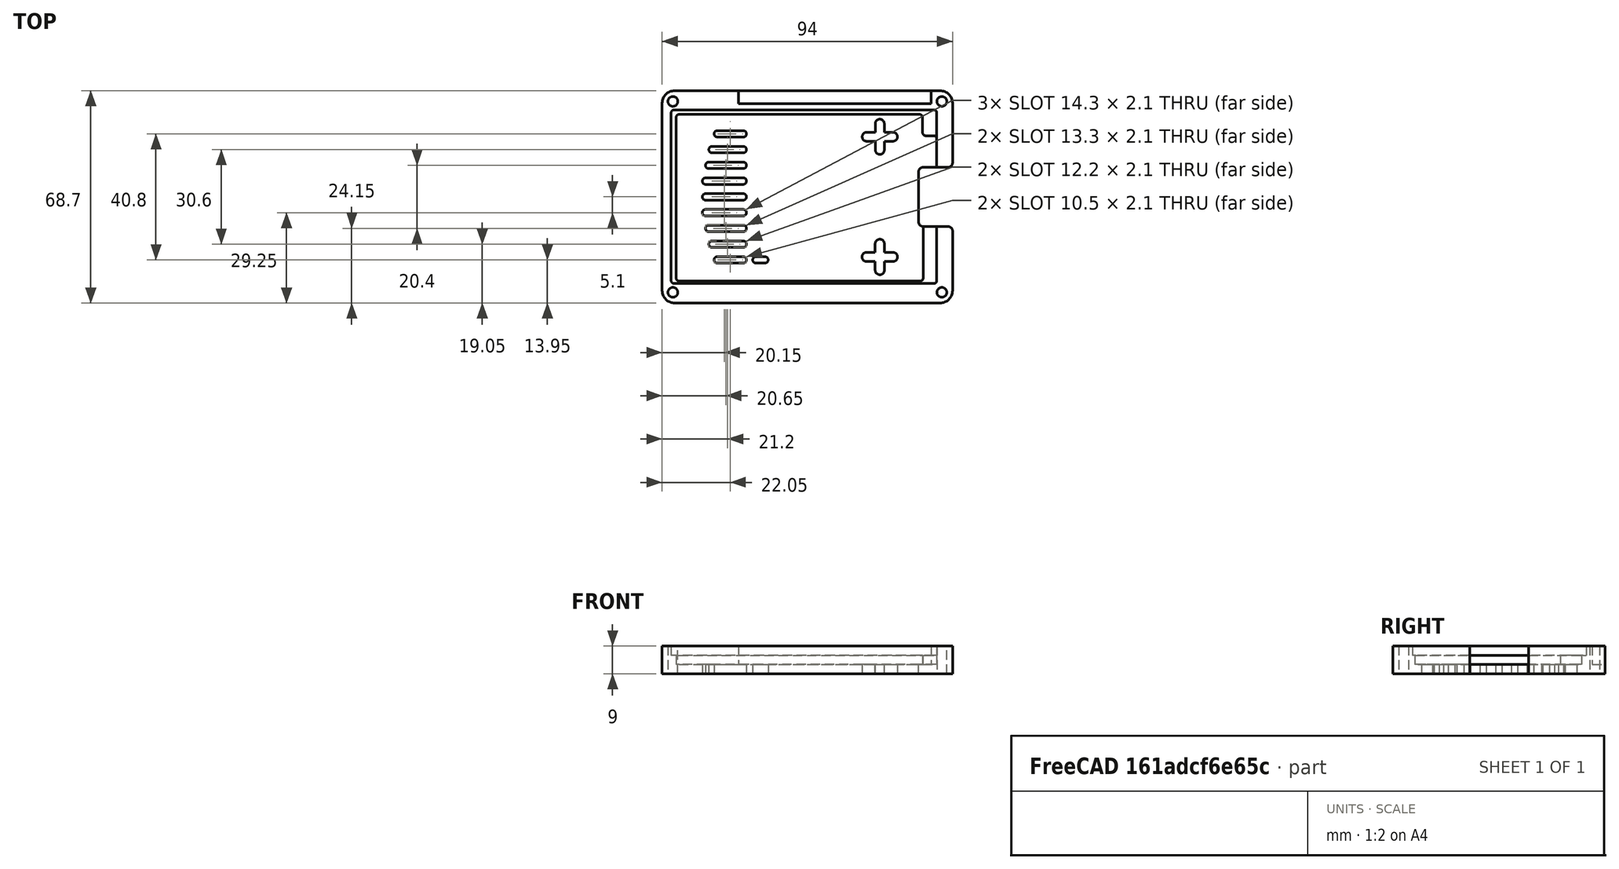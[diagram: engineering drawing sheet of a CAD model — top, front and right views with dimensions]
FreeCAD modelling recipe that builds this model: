
FCSTD DOCUMENT  (FreeCAD 0.19R24267 +148 (Git))
Label: 3. Lage
License: All rights reserved
LicenseURL: http://en.wikipedia.org/wiki/All_rights_reserved
objects: TechDraw::DrawViewDimension×23, Sketcher::SketchObject×3, TechDraw::DrawProjGroupItem×3, PartDesign::Pocket×2, PartDesign::Pad×1, PartDesign::Fillet×1, PartDesign::Body×1, TechDraw::DrawSVGTemplate×1, TechDraw::DrawProjGroup×1, TechDraw::DrawPage×1
note: 12 computed .brp shape members not serialized (recipe doc carries the construction recipe); baked Part::Feature solids carry a one-line shape summary decoded from their .brp

FEATURE [Sketcher::SketchObject] Sketch
  FullyConstrained = true
  MapMode = 5
  Support = -> [XY_Plane]
  sketch-geometry (97):
    g0: LineSegment StartX=0 StartY=0 StartZ=0 EndX=94 EndY=0 EndZ=0
    g1: LineSegment StartX=94 StartY=68.7 StartZ=0 EndX=0 EndY=68.7 EndZ=0
    g2: LineSegment StartX=0 StartY=68.7 StartZ=0 EndX=0 EndY=0 EndZ=0
    g3: GeomPoint X=47 Y=34.35 Z=0
    g4: Circle CenterX=3.45 CenterY=65.25 CenterZ=0 NormalX=0 NormalY=0 NormalZ=1 AngleXU=0 Radius=1.6
    g5: Circle CenterX=90.55 CenterY=65.25 CenterZ=0 NormalX=0 NormalY=0 NormalZ=1 AngleXU=0 Radius=1.6
    g6: Circle CenterX=90.55 CenterY=3.45 CenterZ=0 NormalX=0 NormalY=0 NormalZ=1 AngleXU=0 Radius=1.6
    g7: Circle CenterX=3.45 CenterY=3.45 CenterZ=0 NormalX=0 NormalY=0 NormalZ=1 AngleXU=0 Radius=1.6
    g8: LineSegment StartX=0 StartY=34.35 StartZ=0 EndX=94 EndY=34.35 EndZ=0
    g9: ArcOfCircle CenterX=70.45 CenterY=10.65 CenterZ=0 NormalX=0 NormalY=0 NormalZ=1 AngleXU=0 Radius=1.5 StartAngle=3.14159 EndAngle=6.28319
    g10: ArcOfCircle CenterX=74.7 CenterY=14.9 CenterZ=0 NormalX=0 NormalY=0 NormalZ=1 AngleXU=0 Radius=1.5 StartAngle=4.71239 EndAngle=7.85398
    g11: ArcOfCircle CenterX=70.45 CenterY=19.15 CenterZ=0 NormalX=0 NormalY=0 NormalZ=1 AngleXU=0 Radius=1.5 StartAngle=0 EndAngle=3.14159
    g12: ArcOfCircle CenterX=66.2 CenterY=14.9 CenterZ=0 NormalX=0 NormalY=0 NormalZ=1 AngleXU=0 Radius=1.5 StartAngle=1.5708 EndAngle=4.71239
    g13: LineSegment StartX=66.2 StartY=16.4 StartZ=0 EndX=68.95 EndY=16.4 EndZ=0
    g14: LineSegment StartX=68.95 StartY=16.4 StartZ=0 EndX=68.95 EndY=19.15 EndZ=0
    g15: LineSegment StartX=71.95 StartY=19.15 StartZ=0 EndX=71.95 EndY=16.4 EndZ=0
    g16: LineSegment StartX=71.95 StartY=16.4 StartZ=0 EndX=74.7 EndY=16.4 EndZ=0
    g17: LineSegment StartX=74.7 StartY=13.4 StartZ=0 EndX=71.95 EndY=13.4 EndZ=0
    g18: LineSegment StartX=71.95 StartY=13.4 StartZ=0 EndX=71.95 EndY=10.65 EndZ=0
    g19: LineSegment StartX=68.95 StartY=10.65 StartZ=0 EndX=68.95 EndY=13.4 EndZ=0
    g20: LineSegment StartX=68.95 StartY=13.4 StartZ=0 EndX=66.2 EndY=13.4 EndZ=0
    g21: ArcOfCircle CenterX=70.45 CenterY=49.55 CenterZ=0 NormalX=0 NormalY=0 NormalZ=1 AngleXU=0 Radius=1.45 StartAngle=3.14159 EndAngle=6.28319
    g22: ArcOfCircle CenterX=74.7 CenterY=53.8 CenterZ=0 NormalX=0 NormalY=0 NormalZ=1 AngleXU=0 Radius=1.45 StartAngle=4.71239 EndAngle=7.85398
    g23: ArcOfCircle CenterX=70.45 CenterY=58.05 CenterZ=0 NormalX=0 NormalY=0 NormalZ=1 AngleXU=0 Radius=1.45 StartAngle=7e-16 EndAngle=3.14159
    g24: ArcOfCircle CenterX=66.2 CenterY=53.8 CenterZ=0 NormalX=0 NormalY=0 NormalZ=1 AngleXU=0 Radius=1.45 StartAngle=1.5708 EndAngle=4.71239
    g25: LineSegment StartX=66.2 StartY=55.25 StartZ=0 EndX=69 EndY=55.25 EndZ=0
    g26: LineSegment StartX=69 StartY=55.25 StartZ=0 EndX=69 EndY=58.05 EndZ=0
    g27: LineSegment StartX=71.9 StartY=58.05 StartZ=0 EndX=71.9 EndY=55.25 EndZ=0
    g28: LineSegment StartX=71.9 StartY=55.25 StartZ=0 EndX=74.7 EndY=55.25 EndZ=0
    g29: LineSegment StartX=74.7 StartY=52.35 StartZ=0 EndX=71.9 EndY=52.35 EndZ=0
    g30: LineSegment StartX=71.9 StartY=52.35 StartZ=0 EndX=71.9 EndY=49.55 EndZ=0
    g31: LineSegment StartX=69 StartY=49.55 StartZ=0 EndX=69 EndY=52.35 EndZ=0
    g32: LineSegment StartX=69 StartY=52.35 StartZ=0 EndX=66.2 EndY=52.35 EndZ=0
    g33: LineSegment StartX=94 StartY=0 StartZ=0 EndX=94 EndY=23.275 EndZ=0
    g34: ArcOfCircle CenterX=92.5 CenterY=23.275 CenterZ=0 NormalX=0 NormalY=0 NormalZ=1 AngleXU=0 Radius=1.5 StartAngle=-9e-16 EndAngle=1.5708
    g35: LineSegment StartX=92.5 StartY=24.775 StartZ=0 EndX=84.5 EndY=24.775 EndZ=0
    g36: ArcOfCircle CenterX=84.5 CenterY=26.275 CenterZ=0 NormalX=0 NormalY=0 NormalZ=1 AngleXU=0 Radius=1.5 StartAngle=3.14159 EndAngle=4.71239
    g37: LineSegment StartX=83 StartY=26.275 StartZ=0 EndX=83 EndY=42.425 EndZ=0
    g38: ArcOfCircle CenterX=84.5 CenterY=42.425 CenterZ=0 NormalX=0 NormalY=0 NormalZ=1 AngleXU=0 Radius=1.5 StartAngle=1.5708 EndAngle=3.14159
    g39: LineSegment StartX=84.5 StartY=43.925 StartZ=0 EndX=92.5 EndY=43.925 EndZ=0
    g40: ArcOfCircle CenterX=92.5 CenterY=45.425 CenterZ=0 NormalX=0 NormalY=0 NormalZ=1 AngleXU=0 Radius=1.5 StartAngle=4.71239 EndAngle=6.28319
    g41: LineSegment StartX=94 StartY=45.425 StartZ=0 EndX=94 EndY=68.7 EndZ=0
    g42: LineSegment StartX=27.3 StartY=68.7 StartZ=0 EndX=27.3 EndY=0 EndZ=0
    g43: ArcOfCircle CenterX=14.05 CenterY=29.25 CenterZ=0 NormalX=0 NormalY=0 NormalZ=1 AngleXU=0 Radius=1.05 StartAngle=1.5708 EndAngle=4.71239
    g44: ArcOfCircle CenterX=26.25 CenterY=29.25 CenterZ=0 NormalX=0 NormalY=0 NormalZ=1 AngleXU=0 Radius=1.05 StartAngle=4.71239 EndAngle=7.85398
    g45: LineSegment StartX=14.05 StartY=28.2 StartZ=0 EndX=26.25 EndY=28.2 EndZ=0
    g46: LineSegment StartX=14.05 StartY=30.3 StartZ=0 EndX=26.25 EndY=30.3 EndZ=0
    g47: ArcOfCircle CenterX=14.05 CenterY=34.35 CenterZ=0 NormalX=0 NormalY=0 NormalZ=1 AngleXU=0 Radius=1.05 StartAngle=1.5708 EndAngle=4.71239
    g48: ArcOfCircle CenterX=26.25 CenterY=34.35 CenterZ=0 NormalX=0 NormalY=0 NormalZ=1 AngleXU=0 Radius=1.05 StartAngle=4.71239 EndAngle=7.85398
    g49: LineSegment StartX=14.05 StartY=33.3 StartZ=0 EndX=26.25 EndY=33.3 EndZ=0
    g50: LineSegment StartX=14.05 StartY=35.4 StartZ=0 EndX=26.25 EndY=35.4 EndZ=0
    g51: ArcOfCircle CenterX=15.05 CenterY=24.15 CenterZ=0 NormalX=0 NormalY=0 NormalZ=1 AngleXU=0 Radius=1.05 StartAngle=1.5708 EndAngle=4.71239
    g52: ArcOfCircle CenterX=26.25 CenterY=24.15 CenterZ=0 NormalX=0 NormalY=0 NormalZ=1 AngleXU=0 Radius=1.05 StartAngle=4.71239 EndAngle=7.85398
    g53: LineSegment StartX=15.05 StartY=23.1 StartZ=0 EndX=26.25 EndY=23.1 EndZ=0
    g54: LineSegment StartX=15.05 StartY=25.2 StartZ=0 EndX=26.25 EndY=25.2 EndZ=0
    g55: ArcOfCircle CenterX=16.15 CenterY=19.05 CenterZ=0 NormalX=0 NormalY=0 NormalZ=1 AngleXU=0 Radius=1.05 StartAngle=1.5708 EndAngle=4.71239
    g56: ArcOfCircle CenterX=26.25 CenterY=19.05 CenterZ=0 NormalX=0 NormalY=0 NormalZ=1 AngleXU=0 Radius=1.05 StartAngle=4.71239 EndAngle=7.85398
    g57: LineSegment StartX=16.15 StartY=18 StartZ=0 EndX=26.25 EndY=18 EndZ=0
    g58: LineSegment StartX=16.15 StartY=20.1 StartZ=0 EndX=26.25 EndY=20.1 EndZ=0
    g59: ArcOfCircle CenterX=17.85 CenterY=13.95 CenterZ=0 NormalX=0 NormalY=0 NormalZ=1 AngleXU=0 Radius=1.05 StartAngle=1.5708 EndAngle=4.71239
    g60: ArcOfCircle CenterX=26.25 CenterY=13.95 CenterZ=0 NormalX=0 NormalY=0 NormalZ=1 AngleXU=0 Radius=1.05 StartAngle=4.71239 EndAngle=7.85398
    g61: LineSegment StartX=17.85 StartY=12.9 StartZ=0 EndX=26.25 EndY=12.9 EndZ=0
    g62: LineSegment StartX=17.85 StartY=15 StartZ=0 EndX=26.25 EndY=15 EndZ=0
    g63: ArcOfCircle CenterX=14.05 CenterY=39.45 CenterZ=0 NormalX=0 NormalY=0 NormalZ=1 AngleXU=0 Radius=1.05 StartAngle=1.5708 EndAngle=4.71239
    g64: ArcOfCircle CenterX=26.25 CenterY=39.45 CenterZ=0 NormalX=0 NormalY=0 NormalZ=1 AngleXU=0 Radius=1.05 StartAngle=4.71239 EndAngle=7.85398
    g65: LineSegment StartX=14.05 StartY=38.4 StartZ=0 EndX=26.25 EndY=38.4 EndZ=0
    g66: LineSegment StartX=14.05 StartY=40.5 StartZ=0 EndX=26.25 EndY=40.5 EndZ=0
    g67: ArcOfCircle CenterX=15.05 CenterY=44.55 CenterZ=0 NormalX=0 NormalY=0 NormalZ=1 AngleXU=0 Radius=1.05 StartAngle=1.5708 EndAngle=4.71239
    g68: ArcOfCircle CenterX=26.25 CenterY=44.55 CenterZ=0 NormalX=0 NormalY=0 NormalZ=1 AngleXU=0 Radius=1.05 StartAngle=4.71239 EndAngle=7.85398
    g69: LineSegment StartX=15.05 StartY=43.5 StartZ=0 EndX=26.25 EndY=43.5 EndZ=0
    g70: LineSegment StartX=15.05 StartY=45.6 StartZ=0 EndX=26.25 EndY=45.6 EndZ=0
    g71: ArcOfCircle CenterX=16.15 CenterY=49.65 CenterZ=0 NormalX=0 NormalY=0 NormalZ=1 AngleXU=0 Radius=1.05 StartAngle=1.5708 EndAngle=4.71239
    g72: ArcOfCircle CenterX=26.25 CenterY=49.65 CenterZ=0 NormalX=0 NormalY=0 NormalZ=1 AngleXU=0 Radius=1.05 StartAngle=4.71239 EndAngle=7.85398
    g73: LineSegment StartX=16.15 StartY=48.6 StartZ=0 EndX=26.25 EndY=48.6 EndZ=0
    g74: LineSegment StartX=16.15 StartY=50.7 StartZ=0 EndX=26.25 EndY=50.7 EndZ=0
    g75: ArcOfCircle CenterX=17.85 CenterY=54.75 CenterZ=0 NormalX=0 NormalY=0 NormalZ=1 AngleXU=0 Radius=1.05 StartAngle=1.5708 EndAngle=4.71239
    g76: ArcOfCircle CenterX=26.25 CenterY=54.75 CenterZ=0 NormalX=0 NormalY=0 NormalZ=1 AngleXU=0 Radius=1.05 StartAngle=4.71239 EndAngle=7.85398
    g77: LineSegment StartX=17.85 StartY=53.7 StartZ=0 EndX=26.25 EndY=53.7 EndZ=0
    g78: LineSegment StartX=17.85 StartY=55.8 StartZ=0 EndX=26.25 EndY=55.8 EndZ=0
    g79: ArcOfCircle CenterX=30.35 CenterY=13.95 CenterZ=0 NormalX=0 NormalY=0 NormalZ=1 AngleXU=0 Radius=1.05 StartAngle=1.5708 EndAngle=4.71239
    g80: ArcOfCircle CenterX=33.25 CenterY=13.95 CenterZ=0 NormalX=0 NormalY=0 NormalZ=1 AngleXU=0 Radius=1.05 StartAngle=4.71239 EndAngle=7.85398
    g81: LineSegment StartX=30.35 StartY=12.9 StartZ=0 EndX=33.25 EndY=12.9 EndZ=0
    g82: LineSegment StartX=30.35 StartY=15 StartZ=0 EndX=33.25 EndY=15 EndZ=0
    g83: GeomPoint X=27.3 Y=54.75 Z=0
    g84: GeomPoint X=27.3 Y=49.65 Z=0
    g85: GeomPoint X=27.3 Y=44.55 Z=0
    g86: GeomPoint X=27.3 Y=39.45 Z=0
    g87: GeomPoint X=27.3 Y=34.35 Z=0
    g88: GeomPoint X=27.3 Y=29.25 Z=0
    g89: GeomPoint X=27.3 Y=24.15 Z=0
    g90: GeomPoint X=27.3 Y=19.05 Z=0
    g91: GeomPoint X=27.3 Y=13.95 Z=0
    g92: GeomPoint X=29.3 Y=13.95 Z=0
    g93: LineSegment StartX=26.25 StartY=33.3 StartZ=0 EndX=26.25 EndY=30.3 EndZ=0
    g94: LineSegment StartX=26.25 StartY=28.2 StartZ=0 EndX=26.25 EndY=25.2 EndZ=0
    g95: LineSegment StartX=26.25 StartY=23.1 StartZ=0 EndX=26.25 EndY=20.1 EndZ=0
    g96: LineSegment StartX=26.25 StartY=18 StartZ=0 EndX=26.25 EndY=15 EndZ=0
  constraints (247):
    c: Coincident(g1,g2)
    c: Coincident(g2,g0)
    c: Horizontal(g0)
    c: Horizontal(g1)
    c: Vertical(g2)
    c: Coincident(g0,g-1)
    c: DistanceX(g1,g1) = 94
    c: DistanceY(g2,g2) = 68.7
    c: Symmetric(g1,g0,g3)
    c: Equal(g7,g4)
    c: Equal(g4,g5)
    c: Equal(g5,g6)
    c: Symmetric(g7,g5,g3)
    c: Symmetric(g4,g6,g3)
    c: Radius(g6) = 1.6
    c: Vertical(g7,g4)
    c: Horizontal(g7,g6)
    c: DistanceY(g0,g7) = 3.45
    c: DistanceX(g0,g7) = 3.45
    c: Horizontal(g8)
    c: PointOnObject(g3,g8)
    c: Vertical(g8,g0)
    c: Vertical(g8,g0)
    c: Horizontal(g11,g11)
    c: Horizontal(g11,g11)
    c: Vertical(g10,g10)
    c: Vertical(g10,g10)
    c: Vertical(g12,g12)
    c: Vertical(g12,g12)
    c: Horizontal(g9,g9)
    c: Horizontal(g9,g9)
    c: Equal(g12,g11)
    c: Equal(g11,g10)
    c: Equal(g10,g9)
    c: Tangent(g12,g13) = 1.5708
    c: Coincident(g13,g14)
    c: Coincident(g14,g11)
    c: Vertical(g14)
    c: Tangent(g11,g15) = 1.5708
    c: Coincident(g15,g16)
    c: Coincident(g16,g10)
    c: Tangent(g10,g17) = 1.5708
    c: Coincident(g17,g18)
    c: Coincident(g18,g9)
    c: Tangent(g9,g19) = 1.5708
    c: Coincident(g19,g20)
    c: Coincident(g20,g12)
    c: Equal(g20,g13)
    c: Equal(g13,g14)
    c: Equal(g14,g15)
    c: Equal(g15,g16)
    c: Equal(g16,g17)
    c: Equal(g17,g18)
    c: Equal(g18,g19)
    c: Horizontal(g20)
    c: DistanceX(g13,g15) = 3
    c: DistanceX(g12,g10) = 8.5
    c: Horizontal(g23,g23)
    c: Horizontal(g23,g23)
    c: Vertical(g22,g22)
    c: Vertical(g22,g22)
    c: Vertical(g24,g24)
    c: Vertical(g24,g24)
    c: Horizontal(g21,g21)
    c: Horizontal(g21,g21)
    c: Equal(g24,g23)
    c: Equal(g23,g22)
    c: Equal(g22,g21)
    c: Tangent(g24,g25) = 1.5708
    c: Coincident(g25,g26)
    c: Coincident(g26,g23)
    c: Vertical(g26)
    c: Tangent(g23,g27) = 1.5708
    c: Coincident(g27,g28)
    c: Coincident(g28,g22)
    c: Tangent(g22,g29) = 1.5708
    c: Coincident(g29,g30)
    c: Coincident(g30,g21)
    c: Tangent(g21,g31) = 1.5708
    c: Coincident(g31,g32)
    c: Coincident(g32,g24)
    c: Equal(g32,g25)
    c: Equal(g25,g26)
    c: Equal(g26,g27)
    c: Equal(g27,g28)
    c: Equal(g28,g29)
    c: Equal(g29,g30)
    c: Equal(g30,g31)
    c: Horizontal(g32)
    c: DistanceX(g25,g27) = 2.9
    c: DistanceX(g24,g22) = 8.5
    c: Symmetric(g21,g11,g8)
    c: DistanceY(g0,g9) = 10.65
    c: DistanceX(g10,g0) = 19.3
    c: Coincident(g0,g33)
    c: Vertical(g33)
    c: Tangent(g33,g34) = -1.5708
    c: Coincident(g34,g35)
    c: Horizontal(g35)
    c: Tangent(g35,g36) = 1.5708
    c: Coincident(g36,g37)
    c: Tangent(g37,g38) = 1.5708
    c: Coincident(g38,g39)
    c: Horizontal(g39)
    c: Tangent(g39,g40) = -1.5708
    c: Coincident(g40,g41)
    c: Coincident(g41,g1)
    c: Vertical(g41)
    c: Equal(g38,g40)
    c: Equal(g40,g34)
    c: Equal(g34,g36)
    c: Radius(g40) = 1.5
    c: Vertical(g34,g34)
    c: Horizontal(g36,g36)
    c: Vertical(g38,g38)
    c: Horizontal(g40,g40)
    c: Vertical(g40,g33)
    c: Symmetric(g36,g38,g8)
    c: DistanceY(g34,g39) = 19.15
    c: DistanceX(g37,g40) = 11
    c: Symmetric(g42,g42,g8)
    c: PointOnObject(g42,g0)
    c: DistanceX(g0,g42) = 27.3
    c: Tangent(g43,g46) = 1.5708
    c: Tangent(g43,g45) = -1.5708
    c: Tangent(g45,g44) = -1.5708
    c: Tangent(g46,g44) = 1.5708
    c: Horizontal(g45)
    c: Equal(g43,g44)
    c: Tangent(g47,g50) = 1.5708
    c: Tangent(g47,g49) = -1.5708
    c: Tangent(g49,g48) = -1.5708
    c: Tangent(g50,g48) = 1.5708
    c: Horizontal(g49)
    c: Equal(g47,g48)
    c: PointOnObject(g47,g8)
    c: Tangent(g51,g54) = 1.5708
    c: Tangent(g51,g53) = -1.5708
    c: Tangent(g53,g52) = -1.5708
    c: Tangent(g54,g52) = 1.5708
    c: Horizontal(g53)
    c: Equal(g51,g52)
    c: Tangent(g55,g58) = 1.5708
    c: Tangent(g55,g57) = -1.5708
    c: Tangent(g57,g56) = -1.5708
    c: Tangent(g58,g56) = 1.5708
    c: Horizontal(g57)
    c: Equal(g55,g56)
    c: Tangent(g59,g62) = 1.5708
    c: Tangent(g59,g61) = -1.5708
    c: Tangent(g61,g60) = -1.5708
    c: Tangent(g62,g60) = 1.5708
    c: Horizontal(g61)
    c: Equal(g59,g60)
    c: Tangent(g63,g66) = 1.5708
    c: Tangent(g63,g65) = -1.5708
    c: Tangent(g65,g64) = -1.5708
    c: Tangent(g66,g64) = 1.5708
    c: Horizontal(g65)
    c: Equal(g63,g64)
    c: Tangent(g67,g70) = 1.5708
    c: Tangent(g67,g69) = -1.5708
    c: Tangent(g69,g68) = -1.5708
    c: Tangent(g70,g68) = 1.5708
    c: Horizontal(g69)
    c: Equal(g67,g68)
    c: Tangent(g71,g74) = 1.5708
    c: Tangent(g71,g73) = -1.5708
    c: Tangent(g73,g72) = -1.5708
    c: Tangent(g74,g72) = 1.5708
    c: Horizontal(g73)
    c: Equal(g71,g72)
    c: Tangent(g75,g78) = 1.5708
    c: Tangent(g75,g77) = -1.5708
    c: Tangent(g77,g76) = -1.5708
    c: Tangent(g78,g76) = 1.5708
    c: Horizontal(g77)
    c: Equal(g75,g76)
    c: Tangent(g79,g82) = 1.5708
    c: Tangent(g79,g81) = -1.5708
    c: Tangent(g81,g80) = -1.5708
    c: Tangent(g82,g80) = 1.5708
    c: Horizontal(g81)
    c: Equal(g79,g80)
    c: PointOnObject(g83,g76)
    c: PointOnObject(g84,g72)
    c: PointOnObject(g85,g68)
    c: PointOnObject(g86,g64)
    c: PointOnObject(g87,g48)
    c: PointOnObject(g88,g44)
    c: PointOnObject(g89,g52)
    c: PointOnObject(g90,g56)
    c: PointOnObject(g91,g60)
    c: PointOnObject(g92,g79)
    c: Horizontal(g79,g92)
    c: Horizontal(g92,g91)
    c: Horizontal(g91,g60)
    c: Horizontal(g56,g90)
    c: Horizontal(g52,g89)
    c: Horizontal(g44,g88)
    c: Horizontal(g48,g87)
    c: Horizontal(g64,g86)
    c: Horizontal(g68,g85)
    c: Horizontal(g72,g84)
    c: Horizontal(g76,g83)
    c: Equal(g79,g60)
    c: Equal(g60,g56)
    c: Equal(g56,g52)
    c: Equal(g52,g44)
    c: Equal(g44,g48)
    c: Equal(g48,g64)
    c: Equal(g64,g68)
    c: Equal(g68,g72)
    c: Equal(g72,g76)
    c: PointOnObject(g86,g42)
    c: PointOnObject(g85,g42)
    c: PointOnObject(g84,g42)
    c: PointOnObject(g83,g42)
    c: PointOnObject(g87,g42)
    c: PointOnObject(g88,g42)
    c: PointOnObject(g89,g42)
    c: PointOnObject(g90,g42)
    c: PointOnObject(g91,g42)
    c: Radius(g55) = 1.05
    c: Equal(g65,g50)
    c: DistanceX(g66,g66) = 12.2
    c: DistanceX(g70,g70) = 11.2
    c: DistanceX(g74,g74) = 10.1
    c: Symmetric(g63,g43,g8)
    c: Symmetric(g67,g51,g8)
    c: Symmetric(g71,g55,g8)
    c: Symmetric(g75,g59,g8)
    c: DistanceX(g78,g78) = 8.4
    c: Coincident(g93,g48)
    c: Coincident(g93,g44)
    c: Coincident(g94,g44)
    c: Coincident(g94,g52)
    c: Coincident(g95,g52)
    c: Coincident(g95,g56)
    c: Coincident(g96,g56)
    c: Coincident(g96,g60)
    c: Equal(g96,g95)
    c: Equal(g95,g94)
    c: Equal(g94,g93)
    c: DistanceY(g93,g93) = 3
    c: DistanceX(g82,g82) = 2.9
    c: DistanceX(g91,g92) = 2
FEATURE [PartDesign::Pad] Pad
  Direction = (1,1,1)
  Length = 9
  Length2 = 100
  Profile = -> Sketch
  Type = 0
FEATURE [Sketcher::SketchObject] Sketch001
  ExternalGeometry = -> [Pad]
  FullyConstrained = true
  MapMode = 5
  Placement = pos=(0,0,9) rot=(0,0,1;0rad)
  Support = -> [Pad]
  sketch-geometry (19):
    g0: LineSegment StartX=24.67 StartY=68.7 StartZ=0 EndX=24.67 EndY=64.45 EndZ=0
    g1: LineSegment StartX=24.67 StartY=64.45 StartZ=0 EndX=87.1 EndY=64.45 EndZ=0
    g2: LineSegment StartX=87.1 StartY=64.45 StartZ=0 EndX=87.1 EndY=68.7 EndZ=0
    g3: LineSegment StartX=24.67 StartY=68.7 StartZ=0 EndX=87.1 EndY=68.7 EndZ=0
    g4: LineSegment StartX=4.5 StartY=60.05 StartZ=0 EndX=4.5 EndY=8.1 EndZ=0
    g5: ArcOfCircle CenterX=5.5 CenterY=8.1 CenterZ=0 NormalX=0 NormalY=0 NormalZ=1 AngleXU=0 Radius=1 StartAngle=3.14159 EndAngle=4.71239
    g6: LineSegment StartX=5.5 StartY=7.1 StartZ=0 EndX=83.5 EndY=7.1 EndZ=0
    g7: ArcOfCircle CenterX=83.5 CenterY=8.1 CenterZ=0 NormalX=0 NormalY=0 NormalZ=1 AngleXU=0 Radius=1 StartAngle=4.71239 EndAngle=6.28319
    g8: LineSegment StartX=84.5 StartY=8.1 StartZ=0 EndX=84.5 EndY=24.775 EndZ=0
    g9: LineSegment StartX=84.5 StartY=24.775 StartZ=0 EndX=84.5 EndY=43.925 EndZ=0
    g10: LineSegment StartX=84.5 StartY=43.925 StartZ=0 EndX=88.9 EndY=43.925 EndZ=0
    g11: LineSegment StartX=88.9 StartY=43.925 StartZ=0 EndX=88.9 EndY=53.15 EndZ=0
    g12: ArcOfCircle CenterX=87.9 CenterY=53.15 CenterZ=0 NormalX=0 NormalY=0 NormalZ=1 AngleXU=0 Radius=1 StartAngle=2.24411e-11 EndAngle=1.5708
    g13: LineSegment StartX=87.9 StartY=54.15 StartZ=0 EndX=85.3 EndY=54.15 EndZ=0
    g14: ArcOfCircle CenterX=85.3 CenterY=55.15 CenterZ=0 NormalX=0 NormalY=0 NormalZ=1 AngleXU=0 Radius=1 StartAngle=3.14159 EndAngle=4.71239
    g15: LineSegment StartX=84.3 StartY=55.15 StartZ=0 EndX=84.3 EndY=60.05 EndZ=0
    g16: ArcOfCircle CenterX=83.3 CenterY=60.05 CenterZ=0 NormalX=0 NormalY=0 NormalZ=1 AngleXU=0 Radius=1 StartAngle=1.7e-15 EndAngle=1.5708
    g17: LineSegment StartX=83.3 StartY=61.05 StartZ=0 EndX=5.5 EndY=61.05 EndZ=0
    g18: ArcOfCircle CenterX=5.5 CenterY=60.05 CenterZ=0 NormalX=0 NormalY=0 NormalZ=1 AngleXU=0 Radius=1 StartAngle=1.5708 EndAngle=3.14159
  constraints (55):
    c: PointOnObject(g0,g-3)
    c: Vertical(g0)
    c: Coincident(g0,g1)
    c: Horizontal(g1)
    c: Coincident(g1,g2)
    c: PointOnObject(g2,g-3)
    c: Vertical(g2)
    c: Coincident(g0,g3)
    c: Coincident(g3,g2)
    c: Vertical(g4)
    c: Tangent(g4,g5) = -1.5708
    c: Coincident(g5,g6)
    c: Horizontal(g6)
    c: Tangent(g6,g7) = -1.5708
    c: Coincident(g7,g8)
    c: Vertical(g8)
    c: Coincident(g-8,g8)
    c: Coincident(g9,g8)
    c: Coincident(g9,g10)
    c: PointOnObject(g10,g-7)
    c: Coincident(g10,g11)
    c: Vertical(g11)
    c: Tangent(g11,g12) = -1.5708
    c: Coincident(g12,g13)
    c: Horizontal(g13)
    c: Tangent(g13,g14) = 1.5708
    c: Coincident(g14,g15)
    c: Vertical(g15)
    c: Tangent(g15,g16) = -1.5708
    c: Coincident(g16,g17)
    c: Horizontal(g17)
    c: Tangent(g17,g18) = -1.5708
    c: Horizontal(g18,g18)
    c: Vertical(g16,g16)
    c: Vertical(g12,g12)
    c: Horizontal(g14,g14)
    c: Horizontal(g7,g7)
    c: Vertical(g5,g5)
    c: Coincident(g18,g4)
    c: Equal(g18,g5)
    c: Equal(g5,g7)
    c: Equal(g7,g14)
    c: Equal(g14,g12)
    c: Equal(g12,g16)
    c: DistanceY(g-1,g5) = 7.1
    c: DistanceY(g17,g-5) = 7.65
    c: DistanceX(g-5,g4) = 4.5
    c: DistanceX(g11,g-11) = 5.1
    c: Radius(g12) = 1
    c: Coincident(g9,g-7)
    c: DistanceY(g16,g1) = 3.4
    c: DistanceX(g14,g-11) = 9.7
    c: DistanceY(g13,g1) = 10.3
    c: DistanceX(g3,g3) = 62.43
    c: DistanceX(g2,g-10) = 6.9
FEATURE [PartDesign::Pocket] Pocket
  BaseFeature = -> Pad
  Length = 6
  Length2 = 100
  Profile = -> Sketch001
  Type = 0
FEATURE [Sketcher::SketchObject] Sketch002
  ExternalGeometry = -> [Pocket]
  FullyConstrained = true
  MapMode = 5
  Placement = pos=(0,0,9) rot=(0,0,1;0rad)
  Support = -> [Pocket]
  sketch-geometry (8):
    g0: LineSegment StartX=88.9 StartY=7.29 StartZ=0 EndX=88.9 EndY=61.52 EndZ=0
    g1: ArcOfCircle CenterX=87.9 CenterY=61.52 CenterZ=0 NormalX=0 NormalY=0 NormalZ=1 AngleXU=0 Radius=1 StartAngle=2.5e-15 EndAngle=1.5708
    g2: LineSegment StartX=87.9 StartY=62.52 StartZ=0 EndX=3.9 EndY=62.52 EndZ=0
    g3: ArcOfCircle CenterX=3.9 CenterY=61.52 CenterZ=0 NormalX=0 NormalY=0 NormalZ=1 AngleXU=0 Radius=1 StartAngle=1.5708 EndAngle=3.14159
    g4: LineSegment StartX=2.9 StartY=61.52 StartZ=0 EndX=2.9 EndY=7.29 EndZ=0
    g5: ArcOfCircle CenterX=3.9 CenterY=7.29 CenterZ=0 NormalX=0 NormalY=0 NormalZ=1 AngleXU=0 Radius=1 StartAngle=3.14159 EndAngle=4.71239
    g6: LineSegment StartX=3.9 StartY=6.29 StartZ=0 EndX=87.9 EndY=6.29 EndZ=0
    g7: ArcOfCircle CenterX=87.9 CenterY=7.29 CenterZ=0 NormalX=0 NormalY=0 NormalZ=1 AngleXU=0 Radius=1 StartAngle=4.71239 EndAngle=6.28319
  constraints (24):
    c: Vertical(g0)
    c: Tangent(g0,g1) = -1.5708
    c: Coincident(g1,g2)
    c: Horizontal(g2)
    c: Tangent(g2,g3) = -1.5708
    c: Coincident(g3,g4)
    c: Vertical(g4)
    c: Tangent(g4,g5) = -1.5708
    c: Coincident(g5,g6)
    c: Horizontal(g6)
    c: Tangent(g6,g7) = -1.5708
    c: Coincident(g7,g0)
    c: Vertical(g1,g1)
    c: Horizontal(g3,g3)
    c: Vertical(g5,g5)
    c: Horizontal(g0,g7)
    c: Equal(g7,g5)
    c: Equal(g5,g3)
    c: Equal(g3,g1)
    c: Vertical(g0,g-5)
    c: Radius(g1) = 1
    c: DistanceY(g2,g-3) = 1.93
    c: DistanceX(g-4,g3) = 2.9
    c: DistanceY(g-1,g5) = 6.29
FEATURE [PartDesign::Pocket] Pocket001
  BaseFeature = -> Pocket
  Length = 3
  Length2 = 100
  Profile = -> Sketch002
  Type = 0
FEATURE [PartDesign::Fillet] Fillet
  Base = -> Pocket001 [Edge198,Edge204,Edge203,Edge199]
  BaseFeature = -> Pocket001
  Radius = 4
  SupportTransform = false
FEATURE [PartDesign::Body] Body
  Group = -> [Sketch,Pad,Sketch001,Pocket,Sketch002,Pocket001,Fillet]
  Origin = -> Origin
  Tip = -> Fillet
FEATURE [TechDraw::DrawSVGTemplate] Template
  EditableTexts = Designed_by_Name=Designed by Name; Drawing_number=Drawing number; FC-Date=Date; FC-SC=Scale; FC-SH=Sheet; FC-Title=Title; Subtitle=Subtitle; Weight=Weight
  Height = 210
  Orientation = 1
  Width = 297
FEATURE [TechDraw::DrawProjGroupItem] ProjItem  label="Front"
  CoarseView = false
  Direction = (0,0,1)
  Focus = 100
  HardHidden = false
  IsoCount = 0
  IsoHidden = false
  IsoVisible = false
  LockPosition = true
  Perspective = false
  Rotation = 0
  RotationVector = (1,0,0)
  Scale = 0.5
  ScaleType = 2
  SeamHidden = false
  SeamVisible = true
  SmoothHidden = false
  SmoothVisible = true
  Source = -> [Body]
  Type = 0
  X = 0
  XDirection = (1,0,0)
  Y = 0
FEATURE [TechDraw::DrawProjGroupItem] ProjItem002  label="Right"
  CoarseView = false
  Direction = (1,0,1e-16)
  Focus = 100
  HardHidden = false
  IsoCount = 0
  IsoHidden = false
  IsoVisible = false
  LockPosition = false
  Perspective = false
  Rotation = 0
  RotationVector = (1,0,0)
  Scale = 0.5
  ScaleType = 2
  SeamHidden = false
  SeamVisible = true
  SmoothHidden = false
  SmoothVisible = true
  Source = -> [Body]
  Type = 2
  X = -92.2594
  XDirection = (1e-16,0,-1)
  Y = 0
FEATURE [TechDraw::DrawProjGroupItem] ProjItem003  label="Bottom"
  CoarseView = false
  Direction = (0,-1,0)
  Focus = 100
  HardHidden = false
  IsoCount = 0
  IsoHidden = false
  IsoVisible = false
  LockPosition = false
  Perspective = false
  Rotation = 0
  RotationVector = (1,0,0)
  Scale = 0.5
  ScaleType = 2
  SeamHidden = false
  SeamVisible = true
  SmoothHidden = false
  SmoothVisible = true
  Source = -> [Body]
  Type = 5
  X = 0
  XDirection = (1,0,0)
  Y = 46.2689
FEATURE [TechDraw::DrawProjGroup] ProjGroup
  Anchor = -> ProjItem
  AutoDistribute = true
  LockPosition = false
  ProjectionType = 0
  Rotation = 0
  Scale = 0.5
  ScaleType = 2
  Source = -> [Body]
  Views = -> [ProjItem,ProjItem002,ProjItem003]
  X = 167.951
  Y = 99.9571
  spacingX = 15
  spacingY = 15
FEATURE [TechDraw::DrawViewDimension] Dimension
  Arbitrary = false
  ArbitraryTolerances = false
  EqualTolerance = true
  FormatSpec = %.2f
  FormatSpecOverTolerance = %+.2f
  FormatSpecUnderTolerance = %+.2f
  Inverted = false
  LockPosition = false
  MeasureType = 1
  OverTolerance = 0
  References2D = -> [ProjItem002]
  Rotation = 0
  ScaleType = 0
  TheoreticalExact = false
  Type = 1
  UnderTolerance = 0
  X = 11.8534
  Y = -13.5808
FEATURE [TechDraw::DrawViewDimension] Dimension001
  Arbitrary = false
  ArbitraryTolerances = false
  EqualTolerance = true
  FormatSpec = %.2f
  FormatSpecOverTolerance = %+.2f
  FormatSpecUnderTolerance = %+.2f
  Inverted = false
  LockPosition = false
  MeasureType = 1
  OverTolerance = 0
  References2D = -> [ProjItem002]
  Rotation = 0
  ScaleType = 0
  TheoreticalExact = false
  Type = 2
  UnderTolerance = 0
  X = -11.7327
  Y = -22.8282
FEATURE [TechDraw::DrawViewDimension] Dimension002
  Arbitrary = false
  ArbitraryTolerances = false
  EqualTolerance = true
  FormatSpec = %.2f
  FormatSpecOverTolerance = %+.2f
  FormatSpecUnderTolerance = %+.2f
  Inverted = false
  LockPosition = false
  MeasureType = 1
  OverTolerance = 0
  References2D = -> [ProjItem002]
  Rotation = 0
  ScaleType = 0
  TheoreticalExact = false
  Type = 2
  UnderTolerance = 0
  X = -18.9977
  Y = -9.97973
FEATURE [TechDraw::DrawViewDimension] Dimension003
  Arbitrary = false
  ArbitraryTolerances = false
  EqualTolerance = true
  FormatSpec = %.2f
  FormatSpecOverTolerance = %+.2f
  FormatSpecUnderTolerance = %+.2f
  Inverted = false
  LockPosition = false
  MeasureType = 1
  OverTolerance = 0
  References2D = -> [ProjItem002]
  Rotation = 0
  ScaleType = 0
  TheoreticalExact = false
  Type = 2
  UnderTolerance = 0
  X = -27.5627
  Y = -5.50549
FEATURE [TechDraw::DrawViewDimension] Dimension004
  Arbitrary = false
  ArbitraryTolerances = false
  EqualTolerance = true
  FormatSpec = %.2f
  FormatSpecOverTolerance = %+.2f
  FormatSpecUnderTolerance = %+.2f
  Inverted = false
  LockPosition = false
  MeasureType = 1
  OverTolerance = 0
  References2D = -> [ProjItem002]
  Rotation = 0
  ScaleType = 0
  TheoreticalExact = false
  Type = 2
  UnderTolerance = 0
  X = -34.7001
  Y = -1.24126
FEATURE [TechDraw::DrawViewDimension] Dimension005
  Arbitrary = false
  ArbitraryTolerances = false
  EqualTolerance = true
  FormatSpec = %.2f
  FormatSpecOverTolerance = %+.2f
  FormatSpecUnderTolerance = %+.2f
  Inverted = false
  LockPosition = false
  MeasureType = 1
  OverTolerance = 0
  References2D = -> [ProjItem002]
  Rotation = 0
  ScaleType = 0
  TheoreticalExact = false
  Type = 2
  UnderTolerance = 0
  X = -43.5062
  Y = 3.3777
FEATURE [TechDraw::DrawViewDimension] Dimension006
  Arbitrary = false
  ArbitraryTolerances = false
  EqualTolerance = true
  FormatSpec = %.2f
  FormatSpecOverTolerance = %+.2f
  FormatSpecUnderTolerance = %+.2f
  Inverted = false
  LockPosition = false
  MeasureType = 1
  OverTolerance = 0
  References2D = -> [ProjItem]
  Rotation = 0
  ScaleType = 0
  TheoreticalExact = false
  Type = 1
  UnderTolerance = 0
  X = 16.8336
  Y = -19.713
FEATURE [TechDraw::DrawViewDimension] Dimension007
  Arbitrary = false
  ArbitraryTolerances = false
  EqualTolerance = true
  FormatSpec = R%.2f
  FormatSpecOverTolerance = %+.2f
  FormatSpecUnderTolerance = %+.2f
  Inverted = false
  LockPosition = false
  MeasureType = 1
  OverTolerance = 0
  References2D = -> [ProjItem]
  Rotation = 0
  ScaleType = 0
  TheoreticalExact = false
  Type = 4
  UnderTolerance = 0
  X = 5.20019
  Y = -1.1471
FEATURE [TechDraw::DrawViewDimension] Dimension008
  Arbitrary = false
  ArbitraryTolerances = false
  EqualTolerance = true
  FormatSpec = %.2f
  FormatSpecOverTolerance = %+.2f
  FormatSpecUnderTolerance = %+.2f
  Inverted = false
  LockPosition = false
  MeasureType = 1
  OverTolerance = 0
  References2D = -> [ProjItem]
  Rotation = 0
  ScaleType = 0
  TheoreticalExact = false
  Type = 2
  UnderTolerance = 0
  X = 30.0994
  Y = -9.4756
FEATURE [TechDraw::DrawViewDimension] Dimension009
  Arbitrary = false
  ArbitraryTolerances = false
  EqualTolerance = true
  FormatSpec = %.2f
  FormatSpecOverTolerance = %+.2f
  FormatSpecUnderTolerance = %+.2f
  Inverted = false
  LockPosition = false
  MeasureType = 1
  OverTolerance = 0
  References2D = -> [ProjItem]
  Rotation = 0
  ScaleType = 0
  TheoreticalExact = false
  Type = 2
  UnderTolerance = 0
  X = 39.746
  Y = -10.3854
FEATURE [TechDraw::DrawViewDimension] Dimension010
  Arbitrary = false
  ArbitraryTolerances = false
  EqualTolerance = true
  FormatSpec = %.2f
  FormatSpecOverTolerance = %+.2f
  FormatSpecUnderTolerance = %+.2f
  Inverted = false
  LockPosition = false
  MeasureType = 1
  OverTolerance = 0
  References2D = -> [ProjItem]
  Rotation = 0
  ScaleType = 0
  TheoreticalExact = false
  Type = 2
  UnderTolerance = 0
  X = 51.7676
  Y = -10.1103
FEATURE [TechDraw::DrawViewDimension] Dimension011
  Arbitrary = false
  ArbitraryTolerances = false
  EqualTolerance = true
  FormatSpec = %.2f
  FormatSpecOverTolerance = %+.2f
  FormatSpecUnderTolerance = %+.2f
  Inverted = false
  LockPosition = false
  MeasureType = 1
  OverTolerance = 0
  References2D = -> [ProjItem]
  Rotation = 0
  ScaleType = 0
  TheoreticalExact = false
  Type = 2
  UnderTolerance = 0
  X = 64.2371
  Y = -10.653
FEATURE [TechDraw::DrawViewDimension] Dimension012
  Arbitrary = false
  ArbitraryTolerances = false
  EqualTolerance = true
  FormatSpec = %.2f
  FormatSpecOverTolerance = %+.2f
  FormatSpecUnderTolerance = %+.2f
  Inverted = false
  LockPosition = false
  MeasureType = 1
  OverTolerance = 0
  References2D = -> [ProjItem]
  Rotation = 0
  ScaleType = 0
  TheoreticalExact = false
  Type = 2
  UnderTolerance = 0
  X = 73.6148
  Y = -9.07559
FEATURE [TechDraw::DrawViewDimension] Dimension013
  Arbitrary = false
  ArbitraryTolerances = false
  EqualTolerance = true
  FormatSpec = %.2f
  FormatSpecOverTolerance = %+.2f
  FormatSpecUnderTolerance = %+.2f
  Inverted = false
  LockPosition = false
  MeasureType = 1
  OverTolerance = 0
  References2D = -> [ProjItem]
  Rotation = 0
  ScaleType = 0
  TheoreticalExact = false
  Type = 2
  UnderTolerance = 0
  X = 82.1587
  Y = -1.28475
FEATURE [TechDraw::DrawViewDimension] Dimension014
  Arbitrary = false
  ArbitraryTolerances = false
  EqualTolerance = true
  FormatSpec = %.2f
  FormatSpecOverTolerance = %+.2f
  FormatSpecUnderTolerance = %+.2f
  Inverted = false
  LockPosition = false
  MeasureType = 1
  OverTolerance = 0
  References2D = -> [ProjItem]
  Rotation = 0
  ScaleType = 0
  TheoreticalExact = false
  Type = 1
  UnderTolerance = 0
  X = -2.65582
  Y = -17.5158
FEATURE [TechDraw::DrawViewDimension] Dimension015
  Arbitrary = false
  ArbitraryTolerances = false
  EqualTolerance = true
  FormatSpec = %.2f
  FormatSpecOverTolerance = %+.2f
  FormatSpecUnderTolerance = %+.2f
  Inverted = false
  LockPosition = false
  MeasureType = 1
  OverTolerance = 0
  References2D = -> [ProjItem]
  Rotation = 0
  ScaleType = 0
  TheoreticalExact = false
  Type = 2
  UnderTolerance = 0
  X = -38.4993
  Y = 5.25028
FEATURE [TechDraw::DrawViewDimension] Dimension016
  Arbitrary = false
  ArbitraryTolerances = false
  EqualTolerance = true
  FormatSpec = %.2f
  FormatSpecOverTolerance = %+.2f
  FormatSpecUnderTolerance = %+.2f
  Inverted = false
  LockPosition = false
  MeasureType = 1
  OverTolerance = 0
  References2D = -> [ProjItem]
  Rotation = 0
  ScaleType = 0
  TheoreticalExact = false
  Type = 2
  UnderTolerance = 0
  X = -31.1579
  Y = 7.44296
FEATURE [TechDraw::DrawViewDimension] Dimension017
  Arbitrary = false
  ArbitraryTolerances = false
  EqualTolerance = true
  FormatSpec = %.2f
  FormatSpecOverTolerance = %+.2f
  FormatSpecUnderTolerance = %+.2f
  Inverted = false
  LockPosition = false
  MeasureType = 1
  OverTolerance = 0
  References2D = -> [ProjItem]
  Rotation = 0
  ScaleType = 0
  TheoreticalExact = false
  Type = 2
  UnderTolerance = 0
  X = -45.1338
  Y = 3.48719
FEATURE [TechDraw::DrawViewDimension] Dimension018
  Arbitrary = false
  ArbitraryTolerances = false
  EqualTolerance = true
  FormatSpec = %.2f
  FormatSpecOverTolerance = %+.2f
  FormatSpecUnderTolerance = %+.2f
  Inverted = false
  LockPosition = false
  MeasureType = 1
  OverTolerance = 0
  References2D = -> [ProjItem]
  Rotation = 0
  ScaleType = 0
  TheoreticalExact = false
  Type = 1
  UnderTolerance = 0
  X = 22.7783
  Y = -25.077
FEATURE [TechDraw::DrawViewDimension] Dimension019
  Arbitrary = false
  ArbitraryTolerances = false
  EqualTolerance = true
  FormatSpec = %.2f
  FormatSpecOverTolerance = %+.2f
  FormatSpecUnderTolerance = %+.2f
  Inverted = false
  LockPosition = false
  MeasureType = 1
  OverTolerance = 0
  References2D = -> [ProjItem]
  Rotation = 0
  ScaleType = 0
  TheoreticalExact = false
  Type = 1
  UnderTolerance = 0
  X = -31.8704
  Y = -19.9311
FEATURE [TechDraw::DrawViewDimension] Dimension020
  Arbitrary = false
  ArbitraryTolerances = false
  EqualTolerance = true
  FormatSpec = %.2f
  FormatSpecOverTolerance = %+.2f
  FormatSpecUnderTolerance = %+.2f
  Inverted = false
  LockPosition = false
  MeasureType = 1
  OverTolerance = 0
  References2D = -> [ProjItem]
  Rotation = 0
  ScaleType = 0
  TheoreticalExact = false
  Type = 2
  UnderTolerance = 0
  X = 32.5692
  Y = -22.3871
FEATURE [TechDraw::DrawViewDimension] Dimension021
  Arbitrary = false
  ArbitraryTolerances = false
  EqualTolerance = true
  FormatSpec = %.2f
  FormatSpecOverTolerance = %+.2f
  FormatSpecUnderTolerance = %+.2f
  Inverted = false
  LockPosition = false
  MeasureType = 1
  OverTolerance = 0
  References2D = -> [ProjItem]
  Rotation = 0
  ScaleType = 0
  TheoreticalExact = false
  Type = 2
  UnderTolerance = 0
  X = 13.0614
  Y = 0.327684
FEATURE [TechDraw::DrawViewDimension] Dimension022
  Arbitrary = false
  ArbitraryTolerances = false
  EqualTolerance = true
  FormatSpec = %.2f
  FormatSpecOverTolerance = %+.2f
  FormatSpecUnderTolerance = %+.2f
  Inverted = false
  LockPosition = false
  MeasureType = 1
  OverTolerance = 0
  References2D = -> [ProjItem]
  Rotation = 0
  ScaleType = 0
  TheoreticalExact = false
  Type = 1
  UnderTolerance = 0
  X = -35.1153
  Y = 25.9444
FEATURE [TechDraw::DrawPage] Page
  KeepUpdated = true
  NextBalloonIndex = 1
  ProjectionType = 0
  Template = -> Template
  Views = -> [ProjGroup,Dimension,Dimension001,Dimension002,Dimension003,Dimension004,Dimension005,Dimension006,Dimension007,Dimension008,Dimension009,Dimension010,Dimension011,Dimension012,Dimension013,Dimension014,Dimension015,Dimension016,Dimension017,Dimension018,Dimension019,Dimension020,Dimension021,Dimension022]
